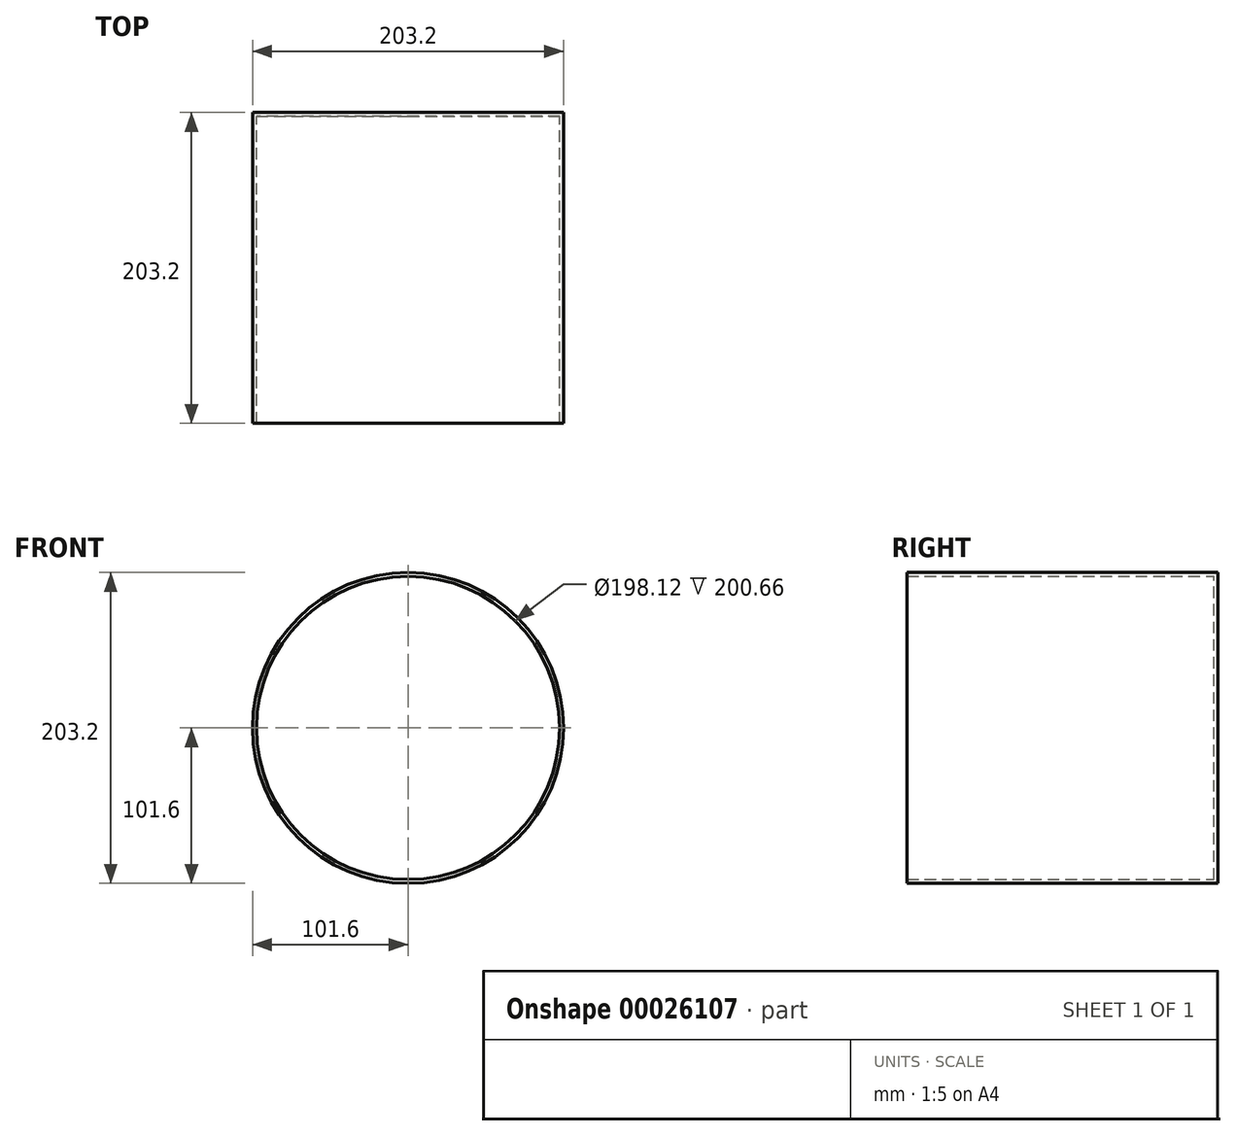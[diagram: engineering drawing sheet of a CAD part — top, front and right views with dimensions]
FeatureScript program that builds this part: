
annotation { "Feature Type Name" : "Feature", "Feature Type Description" : "" }
export const myFeature = defineFeature(function(context is Context, id is Id, definition is map)
    precondition{}
    {
        {
            var Q0;
            Q0=qCreatedBy(makeId("Front.planeOp"),FACE);
            var sketch = newSketch(context, id + "F0", { "sketchPlane" : qUnion([Q0])});
            skCircle(sketch, "E0", {"center": v(0, 0) * mm, "radius": 101.6 * mm});
            skSolve(sketch);
        }
        {
            var Q0;
            Q0=makeQuery(id+"F0.imprint","IMPRINT",FACE,{"disambiguationData":[TD([[makeQuery(id+"F0.imprint","IMPRINT",EDGE,{"derivedFrom":sQuery(id+"F0.wireOp",EDGE,"E0")}),1.0]])]});
            extrude(context, id + "F1", {"entities" : qUnion([Q0]), "depth" : 203.2 * mm});
        }
        {
            var Q0;
            Q0=makeQuery(id+"F1.opExtrude","CAP_FACE",FACE,{"disambiguationData":[OSD([sQuery(id+"F0.wireOp",EDGE,"E0")])],"isStart":false});
            shell(context, id + "F2", {"entities" : qUnion([Q0]), "thickness" : 2.54 * mm});
        }
    });
